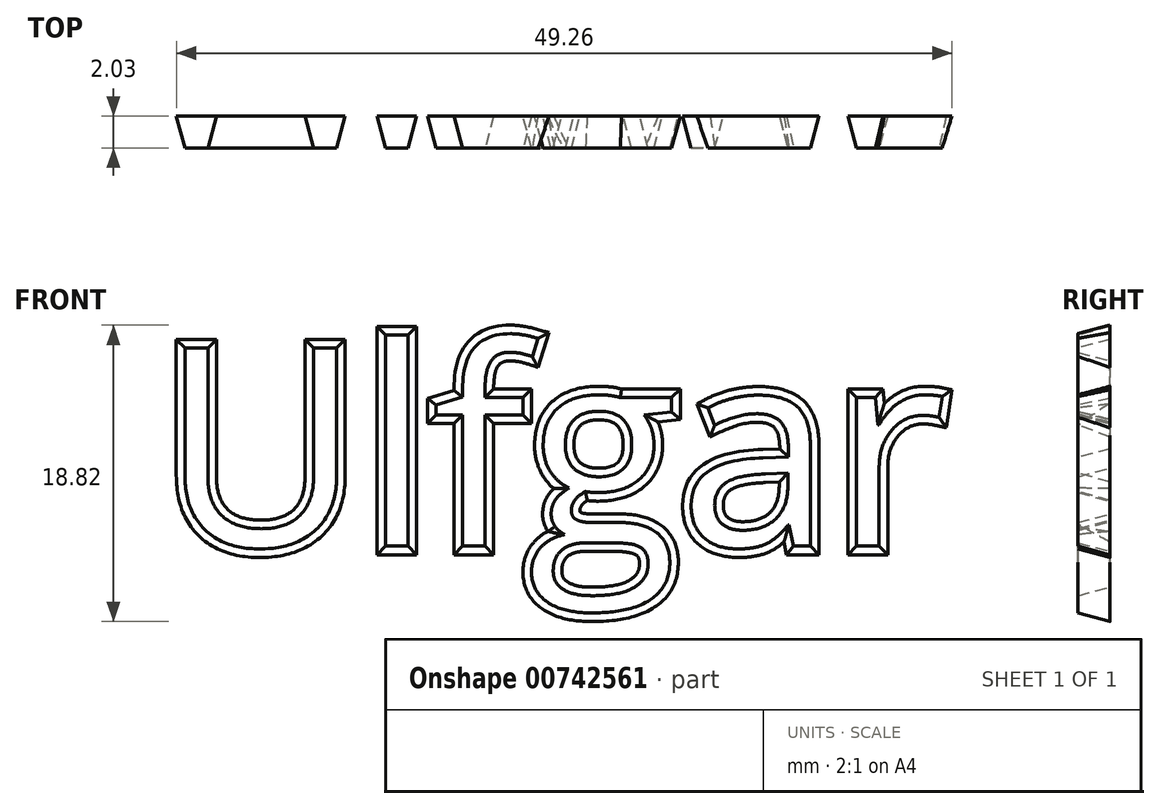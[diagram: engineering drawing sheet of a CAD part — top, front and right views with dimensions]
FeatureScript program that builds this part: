
annotation { "Feature Type Name" : "Feature", "Feature Type Description" : "" }
export const myFeature = defineFeature(function(context is Context, id is Id, definition is map)
    precondition{}
    {
        {
            var Q0;
            Q0=qCreatedBy(makeId("Front.planeOp"),FACE);
            var sketch = newSketch(context, id + "F0", { "sketchPlane" : qUnion([Q0])});
            skLineSegment(sketch, "E0.bottom", {"start": v(-25.4, 15.88) * mm, "end": v(25.4, 15.88) * mm});
            skLineSegment(sketch, "E0.top", {"start": v(-25.4, -15.88) * mm, "end": v(25.4, -15.88) * mm});
            skLineSegment(sketch, "E0.left", {"start": v(-25.4, 15.88) * mm, "end": v(-25.4, -15.88) * mm});
            skLineSegment(sketch, "E0.right", {"start": v(25.4, 15.87) * mm, "end": v(25.4, -15.88) * mm});
            skPoint(sketch, "E0.middle", {"position": v(0, 0) * mm});
            skSolve(sketch);
        }
        {
            var Q0;
            Q0=qCreatedBy(makeId("Front.planeOp"),FACE);
            var sketch = newSketch(context, id + "F1", { "sketchPlane" : qUnion([Q0])});
            skText(sketch, "E1", { "text": "Ulfgar", "fontName": "OpenSans-Regular.ttf"});
            const initialGuessF1  = {"E1": [-0.02542, -0.00635, 1, 0, 0.0127]};
            skSetInitialGuess(sketch, initialGuessF1);
            skSolve(sketch);
        }
        {
            var Q0;
            Q0 = qSketchRegion(id + "F1", true);
            extrude(context, id + "F2", {"entities" : qUnion([Q0]), "oppositeDirection" : true, "depth" : 2.03 * mm, "offsetDistance" : 25.4 * mm, "hasDraft" : true, "draftAngle" : 15 * degree});
        }
    });
